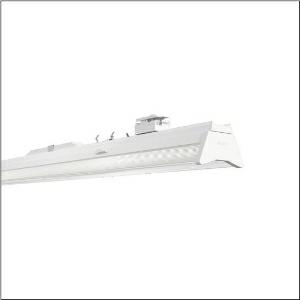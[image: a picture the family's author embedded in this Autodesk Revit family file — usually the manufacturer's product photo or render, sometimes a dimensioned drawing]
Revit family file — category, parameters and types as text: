
# Revit family: licross_r__21_performance_mo_51td16vnd8xg_f547
name_source: partatom
category: Lighting Fixtures
units: mm (PartAtom-declared; Revit-internal decimal feet)

## family parameters
Cut with Voids When Loaded = No
Host = Face
Light Source = No
Part Type = Normal
Room Calculation Point = No
Round Connector Dimension = Use Diameter
Shared = No

## types (1)
- --- (1 x LED, 8000 lm, 48.3 W, 4000K)
    Apparent Load = 48 VA
    CIE Flux Codes = 66 88 96 79 100
    Color Rendering = 90
    Color Temperature = 4000K
    Default Elevation = 1800 mm
    Description = Licross® 21 Performance MO, luminaire insert, of sheet steel, galvanised, coil coated, white, length: 1.500mm, width: 120mm, height: 123mm, LED rated luminous flux: 8.000lm, light colour: 940, control gear: DALI 2, CLO, with plug, 5-pole, with phase selection, mains connection: 220..240V, AC, 50/60Hz, start of lifetime: 48W, end of service life: 53W, internal wiring halogen-free, primary light control with lens, of plastic, primary optical cover: cover, of PMMA, light emission: direct/indirect distribution, primary light characteristic: symmetric, protection rating (complete): IP54, insulation class (complete): insulation class I (protective earthing), certification: CE, ENEC, VDE, UKCA, protection symbol: D if used in an environment with non-conductive dust loads with corresponding accessories, impact resistance: IK06, permissible ambient temperature for indoor applications: -25..+35°C, corresponds to IFS (International Featured Standards) requirements for safety and quality in the food industry, reducing of maximum allowable ambient temperature of 5°C with ceiling mounting, LABS conformity tested according to VDMA 24364:2018-05, packaging unit: 1 piece
    Height = 114 mm
    Lamp = 1 x LED
    Lamp Light Flux = 8000 lm
    Lamp Power = 48.3 W
    Lamp count = 1
    Length = 1500 mm
    Luminous efficacy = 166 lm/W
    Manufacturer = Siteco
    ModVariant = No
    Model = 51TD16VND8XG
    Mounting Place = Ceiling
    Mounting Type = Pendant
    Number of Poles = 1
    OnlyDefault = Yes
    Power Factor = 1
    Product Name = Licross® 21 Performance MO
    Product group = luminaire insert | ceiling pendant
    ProductGroupID = 902
    Protection Class = Protection class I
    Protection Degree = IP 54
    RLX_Detail_Level = 1
    RLX_Emergency_Light_Flux = 0 lm
    RLX_Emergency_Type = 0
    RLX_Emergency_Type_DB = No
    RlxData = <blob elided: 34161 chars, md5=0e5f95fa>
    Socket = socket
    Standby Power = 0 W
    System Light Flux = 8000 lm
    System Power = 48 W
    Type Comments = factory setting: luminous flux: 100 % | dim-lin: 254 | 324 mA
    Type Image = l_1256138.jpg
    URL = http://relux.com
    VarID = @adj_109247
    Voltage = 0 V
    Weight = 0.00 kg
    Width = 120 mm

## geometry (parser evidence)
native form markers: Blend x4, Sweep x14
no freeform markers — native parametric forms only
